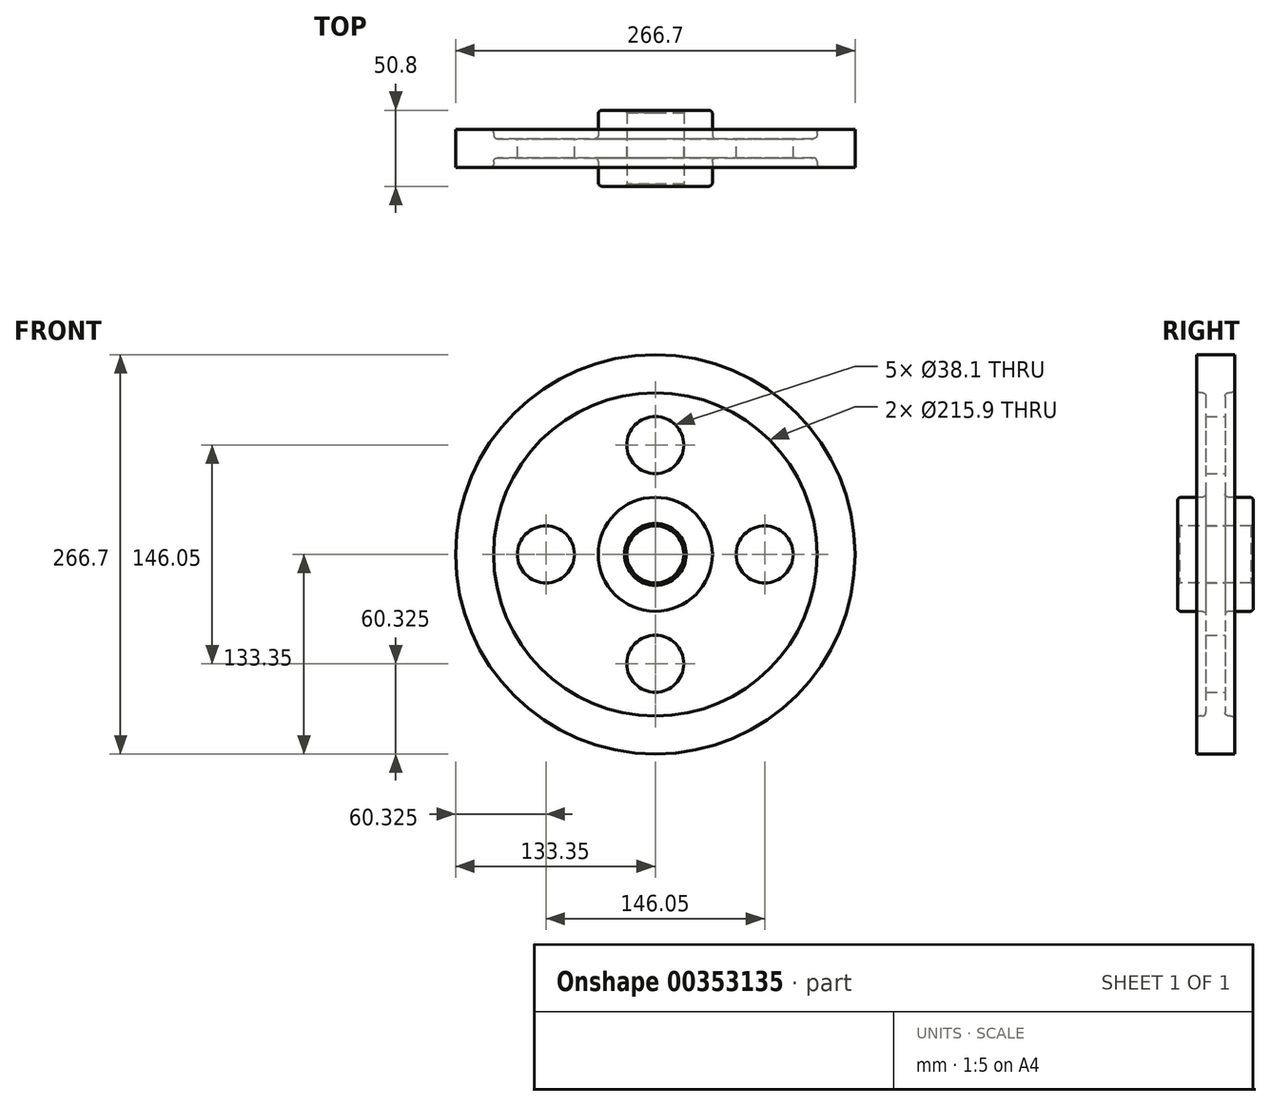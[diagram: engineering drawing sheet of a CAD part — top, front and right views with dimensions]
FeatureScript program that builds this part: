
annotation { "Feature Type Name" : "Feature", "Feature Type Description" : "" }
export const myFeature = defineFeature(function(context is Context, id is Id, definition is map)
    precondition{}
    {
        {
            var Q0;
            Q0=qCreatedBy(makeId("Right.planeOp"),FACE);
            var sketch = newSketch(context, id + "F0", { "sketchPlane" : qUnion([Q0])});
            skLineSegment(sketch, "E0", {"start": v(0, 0) * mm, "end": v(80.43, 0) * mm, "construction": true});
            skLineSegment(sketch, "E1.0", {"start": v(0, 19.05) * mm, "end": v(25.4, 19.05) * mm, "construction": true});
            skLineSegment(sketch, "E2.0", {"start": v(6.35, 38.1) * mm, "end": v(25.4, 38.1) * mm, "construction": true});
            skLineSegment(sketch, "E3.0", {"start": v(6.35, 107.95) * mm, "end": v(12.7, 107.95) * mm, "construction": true});
            skLineSegment(sketch, "E4.0", {"start": v(0, 133.35) * mm, "end": v(12.7, 133.35) * mm, "construction": true});
            skLineSegment(sketch, "E5", {"start": v(0, 133.35) * mm, "end": v(0, 0) * mm, "construction": true});
            skLineSegment(sketch, "E6.0", {"start": v(25.4, 38.1) * mm, "end": v(25.4, 19.05) * mm, "construction": true});
            skLineSegment(sketch, "E7.0", {"start": v(6.35, 107.95) * mm, "end": v(6.35, 38.1) * mm, "construction": true});
            skLineSegment(sketch, "E8.0", {"start": v(12.7, 133.35) * mm, "end": v(12.7, 107.95) * mm, "construction": true});
            skLineSegment(sketch, "E9", {"start": v(0, 133.35) * mm, "end": v(12.7, 133.35) * mm});
            skLineSegment(sketch, "E10", {"start": v(12.7, 107.95) * mm, "end": v(6.35, 107.95) * mm});
            skLineSegment(sketch, "E11", {"start": v(6.35, 107.95) * mm, "end": v(6.35, 38.1) * mm});
            skLineSegment(sketch, "E12", {"start": v(25.4, 38.1) * mm, "end": v(25.4, 19.05) * mm});
            skLineSegment(sketch, "E13", {"start": v(6.35, 38.1) * mm, "end": v(25.4, 38.1) * mm});
            skPoint(sketch, "E14.orphan", {"position": v(0, 107.95) * mm});
            skLineSegment(sketch, "E15", {"start": v(12.7, 133.35) * mm, "end": v(12.7, 107.95) * mm});
            skLineSegment(sketch, "E16", {"start": v(25.4, 19.05) * mm, "end": v(0, 19.05) * mm});
            skLineSegment(sketch, "E17.MirrorCS", {"start": v(-12.7, 133.35) * mm, "end": v(-12.7, 107.95) * mm});
            skLineSegment(sketch, "E18.MirrorCS", {"start": v(-12.7, 107.95) * mm, "end": v(-6.35, 107.95) * mm});
            skLineSegment(sketch, "E19.MirrorCS", {"start": v(-6.35, 107.95) * mm, "end": v(-6.35, 38.1) * mm});
            skLineSegment(sketch, "E20.MirrorCS", {"start": v(-6.35, 38.1) * mm, "end": v(-25.4, 38.1) * mm});
            skLineSegment(sketch, "E21.MirrorCS", {"start": v(-25.4, 38.1) * mm, "end": v(-25.4, 19.05) * mm});
            skLineSegment(sketch, "E22.MirrorCS", {"start": v(-25.4, 19.05) * mm, "end": v(0, 19.05) * mm});
            skLineSegment(sketch, "E23.MirrorCS", {"start": v(0, 133.35) * mm, "end": v(-12.7, 133.35) * mm});
            skSolve(sketch);
        }
        {
            var Q0;
            Q0=makeQuery(id+"F0.imprint","IMPRINT",FACE,{"disambiguationData":[TD([[makeQuery(id+"F0.imprint","IMPRINT",EDGE,{"derivedFrom":sQuery(id+"F0.wireOp",EDGE,"E9")}),-1.0]])]});
            var Q1;
            Q1=sQuery(id+"F0.wireOp",EDGE,"E0");
            revolve(context, id + "F1", {"entities" : qUnion([Q0]), "axis" : qUnion([Q1]), "revolveType" : RevolveType.FULL});
        }
        {
            var Q0;
            Q0=makeQuery(id+"F1.opRevolve","SWEPT_FACE",FACE,{"disambiguationData":[OSD([sQuery(id+"F0.wireOp",EDGE,"E11")])]});
            var sketch = newSketch(context, id + "F2", { "sketchPlane" : qUnion([Q0])});
            skLineSegment(sketch, "E24", {"start": v(0, 0) * mm, "end": v(0, 73.03) * mm});
            skCircle(sketch, "E25", {"center": v(0, 73.03) * mm, "radius": 19.05 * mm});
            skCircle(sketch, "E26.1.0", {"center": v(-73.03, 0) * mm, "radius": 19.05 * mm});
            skCircle(sketch, "E26.2.0", {"center": v(0, -73.03) * mm, "radius": 19.05 * mm});
            skCircle(sketch, "E26.3.0", {"center": v(73.03, 0) * mm, "radius": 19.05 * mm});
            skPoint(sketch, "E26.center", {"position": v(0, 0) * mm});
            skSolve(sketch);
        }
        {
            var Q0;
            Q0 = qSketchRegion(id + "F2", true);
            extrude(context, id + "F3", {"entities" : qUnion([Q0]), "operationType" : NewBodyOperationType.REMOVE, "oppositeDirection" : true, "depth" : 25.4 * mm});
        }
        {
            var Q0;
            Q0=makeQuery(id+"F1.opRevolve","SWEPT_EDGE",EDGE,{"disambiguationData":[OSD([sQuery(id+"F0.wireOp",EDGE,"E18.MirrorCS"),sQuery(id+"F0.wireOp",EDGE,"E19.MirrorCS")])]});
            var Q1;
            Q1=makeQuery(id+"F1.opRevolve","SWEPT_EDGE",EDGE,{"disambiguationData":[OSD([sQuery(id+"F0.wireOp",EDGE,"E17.MirrorCS"),sQuery(id+"F0.wireOp",EDGE,"E18.MirrorCS")])]});
            var Q2;
            Q2=makeQuery(id+"F1.opRevolve","SWEPT_EDGE",EDGE,{"disambiguationData":[OSD([sQuery(id+"F0.wireOp",EDGE,"E19.MirrorCS"),sQuery(id+"F0.wireOp",EDGE,"E20.MirrorCS")])]});
            var Q3;
            Q3=makeQuery(id+"F1.opRevolve","SWEPT_EDGE",EDGE,{"disambiguationData":[OSD([sQuery(id+"F0.wireOp",EDGE,"E20.MirrorCS"),sQuery(id+"F0.wireOp",EDGE,"E21.MirrorCS")])]});
            var Q4;
            Q4=makeQuery(id+"F1.opRevolve","SWEPT_EDGE",EDGE,{"disambiguationData":[OSD([sQuery(id+"F0.wireOp",EDGE,"E10"),sQuery(id+"F0.wireOp",EDGE,"E15")])]});
            var Q5;
            Q5=makeQuery(id+"F1.opRevolve","SWEPT_EDGE",EDGE,{"disambiguationData":[OSD([sQuery(id+"F0.wireOp",EDGE,"E10"),sQuery(id+"F0.wireOp",EDGE,"E11")])]});
            var Q6;
            Q6=makeQuery(id+"F1.opRevolve","SWEPT_EDGE",EDGE,{"disambiguationData":[OSD([sQuery(id+"F0.wireOp",EDGE,"E12"),sQuery(id+"F0.wireOp",EDGE,"E13")])]});
            var Q7;
            Q7=makeQuery(id+"F1.opRevolve","SWEPT_EDGE",EDGE,{"disambiguationData":[OSD([sQuery(id+"F0.wireOp",EDGE,"E11"),sQuery(id+"F0.wireOp",EDGE,"E13")])]});
            fillet(context, id + "F4", {"entities" : qUnion([Q0, Q1, Q2, Q3, Q4, Q5, Q6, Q7]), "radius" : 2.54 * mm, "tangentPropagation" : true, "allowEdgeOverflow" : false});
        }
        {
            var Q0;
            Q0=makeQuery(id+"F1.opRevolve","SWEPT_EDGE",EDGE,{"disambiguationData":[OSD([sQuery(id+"F0.wireOp",EDGE,"E21.MirrorCS"),sQuery(id+"F0.wireOp",EDGE,"E22.MirrorCS")])]});
            var Q1;
            Q1=makeQuery(id+"F1.opRevolve","SWEPT_EDGE",EDGE,{"disambiguationData":[OSD([sQuery(id+"F0.wireOp",EDGE,"E12"),sQuery(id+"F0.wireOp",EDGE,"E16")])]});
            chamfer(context, id + "F5", {"entities" : qUnion([Q0, Q1]), "width" : 1.59 * mm, "tangentPropagation" : true});
        }
    });
